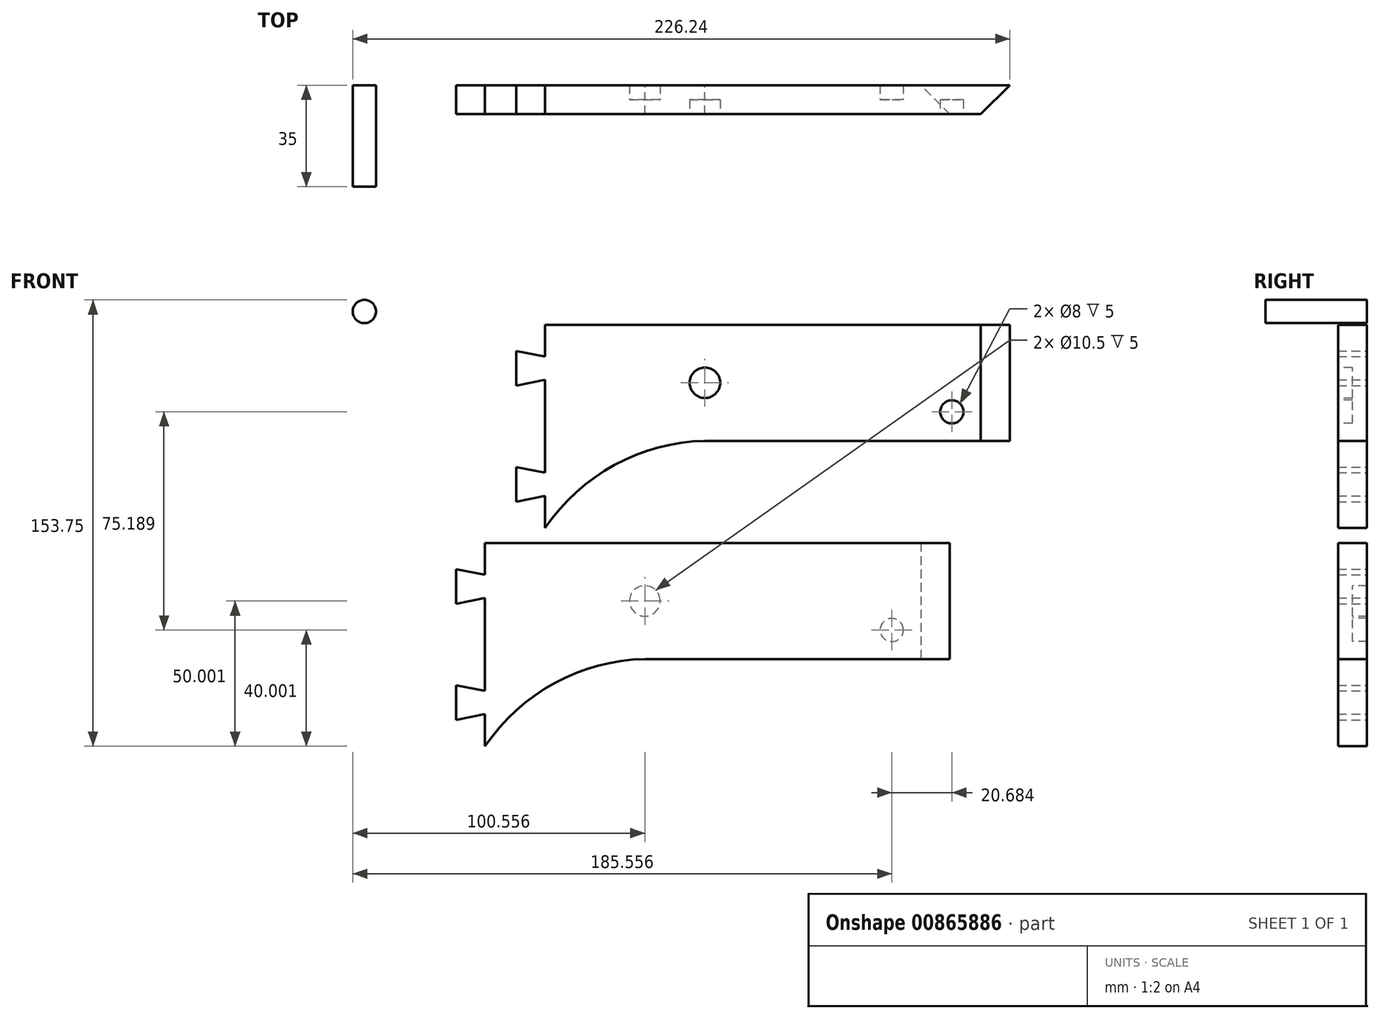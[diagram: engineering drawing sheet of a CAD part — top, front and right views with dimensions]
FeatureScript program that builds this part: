
annotation { "Feature Type Name" : "Feature", "Feature Type Description" : "" }
export const myFeature = defineFeature(function(context is Context, id is Id, definition is map)
    precondition{}
    {
        {
            var Q0;
            Q0=qCreatedBy(makeId("Front.planeOp"),FACE);
            var sketch = newSketch(context, id + "F0", { "sketchPlane" : qUnion([Q0])});
            skLineSegment(sketch, "E0.bottom", {"start": v(65, 0) * mm, "end": v(170, 0) * mm});
            skLineSegment(sketch, "E0.top", {"start": v(10, 40) * mm, "end": v(170, 40) * mm});
            skLineSegment(sketch, "E0.left", {"start": v(0, 19) * mm, "end": v(0, 31) * mm});
            skLineSegment(sketch, "E0.right", {"start": v(170, 0) * mm, "end": v(170, 40) * mm});
            skLineSegment(sketch, "E1", {"start": v(0, -9) * mm, "end": v(0, -21) * mm});
            skLineSegment(sketch, "E2", {"start": v(10, 40) * mm, "end": v(10, 29) * mm});
            skLineSegment(sketch, "E3", {"start": v(0, 31) * mm, "end": v(10, 29) * mm});
            skLineSegment(sketch, "E4", {"start": v(0, 19) * mm, "end": v(10, 21) * mm});
            skLineSegment(sketch, "E5", {"start": v(0, -9) * mm, "end": v(10, -11) * mm});
            skLineSegment(sketch, "E6", {"start": v(0, -21) * mm, "end": v(10, -19) * mm});
            skArc(sketch, "E7", {"start": v(65, 0) * mm, "mid": v(33.88, -8.36) * mm, "end": v(10, -30) * mm});
            skPoint(sketch, "E8.orphan", {"position": v(0, 40) * mm});
            skLineSegment(sketch, "E9.trimOffspring", {"start": v(10, 21) * mm, "end": v(10, -11) * mm});
            skPoint(sketch, "E10.orphan", {"position": v(0, 0) * mm});
            skLineSegment(sketch, "E11.trimOffspring", {"start": v(10, -19) * mm, "end": v(10, -30) * mm});
            skSolve(sketch);
        }
        {
            var Q0;
            Q0 = qSketchRegion(id + "F0", true);
            extrude(context, id + "F1", {"entities" : qUnion([Q0]), "depth" : 10 * mm, "offsetDistance" : 25 * mm});
        }
        {
            var Q0;
            Q0=makeQuery(id+"F1.opExtrude","CAP_FACE",FACE,{"disambiguationData":[OSD([sQuery(id+"F0.wireOp",EDGE,"E0.bottom"),sQuery(id+"F0.wireOp",EDGE,"E0.top"),sQuery(id+"F0.wireOp",EDGE,"E0.left"),sQuery(id+"F0.wireOp",EDGE,"E0.right"),sQuery(id+"F0.wireOp",EDGE,"E1"),sQuery(id+"F0.wireOp",EDGE,"E2"),sQuery(id+"F0.wireOp",EDGE,"E3"),sQuery(id+"F0.wireOp",EDGE,"E4"),sQuery(id+"F0.wireOp",EDGE,"E5"),sQuery(id+"F0.wireOp",EDGE,"E6"),sQuery(id+"F0.wireOp",EDGE,"E7"),sQuery(id+"F0.wireOp",EDGE,"E9.trimOffspring"),sQuery(id+"F0.wireOp",EDGE,"E11.trimOffspring")])],"isStart":false});
            var sketch = newSketch(context, id + "F2", { "sketchPlane" : qUnion([Q0])});
            skCircle(sketch, "E12", {"center": v(65, 20) * mm, "radius": 5.25 * mm});
            skCircle(sketch, "E13", {"center": v(150, 10) * mm, "radius": 4 * mm});
            skSolve(sketch);
        }
        {
            var Q0;
            Q0 = qSketchRegion(id + "F2", true);
            extrude(context, id + "F3", {"entities" : qUnion([Q0]), "operationType" : NewBodyOperationType.REMOVE, "oppositeDirection" : true, "depth" : 5 * mm, "offsetDistance" : 25 * mm});
        }
        {
            var Q0;
            Q0=makeQuery(id+"F1.opExtrude","CAP_EDGE",EDGE,{"disambiguationData":[OSD([sQuery(id+"F0.wireOp",EDGE,"E0.right")])],"isStart":false});
            chamfer(context, id + "F4", {"entities" : qUnion([Q0]), "width" : 10 * mm, "tangentPropagation" : true});
        }
        {
            var Q0;
            Q0=qCreatedBy(makeId("Front.planeOp"),FACE);
            var sketch = newSketch(context, id + "F5", { "sketchPlane" : qUnion([Q0])});
            skLineSegment(sketch, "E14.bottom", {"start": v(44.32, -75.19) * mm, "end": v(149.32, -75.19) * mm});
            skLineSegment(sketch, "E14.top", {"start": v(-10.68, -35.19) * mm, "end": v(149.32, -35.19) * mm});
            skLineSegment(sketch, "E14.left", {"start": v(-20.68, -56.19) * mm, "end": v(-20.68, -44.19) * mm});
            skLineSegment(sketch, "E14.right", {"start": v(149.32, -75.19) * mm, "end": v(149.32, -35.19) * mm});
            skLineSegment(sketch, "E15", {"start": v(-20.68, -84.19) * mm, "end": v(-20.68, -96.19) * mm});
            skLineSegment(sketch, "E16", {"start": v(-10.68, -35.19) * mm, "end": v(-10.68, -46.19) * mm});
            skLineSegment(sketch, "E17", {"start": v(-20.68, -44.19) * mm, "end": v(-10.68, -46.19) * mm});
            skLineSegment(sketch, "E18", {"start": v(-20.68, -56.19) * mm, "end": v(-10.68, -54.19) * mm});
            skLineSegment(sketch, "E19", {"start": v(-20.68, -84.19) * mm, "end": v(-10.68, -86.19) * mm});
            skLineSegment(sketch, "E20", {"start": v(-20.68, -96.19) * mm, "end": v(-10.68, -94.19) * mm});
            skArc(sketch, "E21", {"start": v(44.32, -75.19) * mm, "mid": v(13.2, -83.55) * mm, "end": v(-10.68, -105.19) * mm});
            skPoint(sketch, "E22.orphan", {"position": v(-20.68, -35.19) * mm});
            skLineSegment(sketch, "E23.trimOffspring", {"start": v(-10.68, -54.19) * mm, "end": v(-10.68, -86.19) * mm});
            skPoint(sketch, "E24.orphan", {"position": v(-20.68, -75.19) * mm});
            skLineSegment(sketch, "E25.trimOffspring", {"start": v(-10.68, -94.19) * mm, "end": v(-10.68, -105.19) * mm});
            skSolve(sketch);
        }
        {
            var Q0;
            Q0 = qSketchRegion(id + "F5", true);
            extrude(context, id + "F6", {"entities" : qUnion([Q0]), "depth" : 10 * mm, "offsetDistance" : 25 * mm});
        }
        {
            var Q0;
            Q0=makeQuery(id+"F6.opExtrude","CAP_FACE",FACE,{"disambiguationData":[OSD([sQuery(id+"F5.wireOp",EDGE,"E14.bottom"),sQuery(id+"F5.wireOp",EDGE,"E14.top"),sQuery(id+"F5.wireOp",EDGE,"E14.left"),sQuery(id+"F5.wireOp",EDGE,"E14.right"),sQuery(id+"F5.wireOp",EDGE,"E15"),sQuery(id+"F5.wireOp",EDGE,"E16"),sQuery(id+"F5.wireOp",EDGE,"E17"),sQuery(id+"F5.wireOp",EDGE,"E18"),sQuery(id+"F5.wireOp",EDGE,"E19"),sQuery(id+"F5.wireOp",EDGE,"E20"),sQuery(id+"F5.wireOp",EDGE,"E21"),sQuery(id+"F5.wireOp",EDGE,"E23.trimOffspring"),sQuery(id+"F5.wireOp",EDGE,"E25.trimOffspring")])],"isStart":false});
            var sketch = newSketch(context, id + "F7", { "sketchPlane" : qUnion([Q0])});
            skCircle(sketch, "E26", {"center": v(44.32, -55.19) * mm, "radius": 5.25 * mm});
            skCircle(sketch, "E27", {"center": v(129.32, -65.19) * mm, "radius": 4 * mm});
            skSolve(sketch);
        }
        {
            var Q0;
            Q0 = qSketchRegion(id + "F7", true);
            extrude(context, id + "F8", {"entities" : qUnion([Q0]), "operationType" : NewBodyOperationType.REMOVE, "oppositeDirection" : true, "depth" : 10 * mm, "offsetDistance" : 25 * mm, "hasSecondDirection" : true, "secondDirectionOppositeDirection" : true, "secondDirectionDepth" : 5 * mm});
        }
        {
            var Q0;
            Q0=makeQuery(id+"F6.opExtrude","CAP_EDGE",EDGE,{"disambiguationData":[OSD([sQuery(id+"F5.wireOp",EDGE,"E14.right")])],"isStart":true});
            chamfer(context, id + "F9", {"entities" : qUnion([Q0]), "width" : 10 * mm, "tangentPropagation" : true});
        }
        {
            var Q0;
            Q0=qCreatedBy(makeId("Front.planeOp"),FACE);
            var sketch = newSketch(context, id + "F10", { "sketchPlane" : qUnion([Q0])});
            skCircle(sketch, "E28", {"center": v(-52.24, 44.56) * mm, "radius": 4 * mm});
            skSolve(sketch);
        }
        {
            var Q0;
            Q0 = qSketchRegion(id + "F10", true);
            extrude(context, id + "F11", {"entities" : qUnion([Q0]), "depth" : 35 * mm, "offsetDistance" : 25 * mm});
        }
    });
